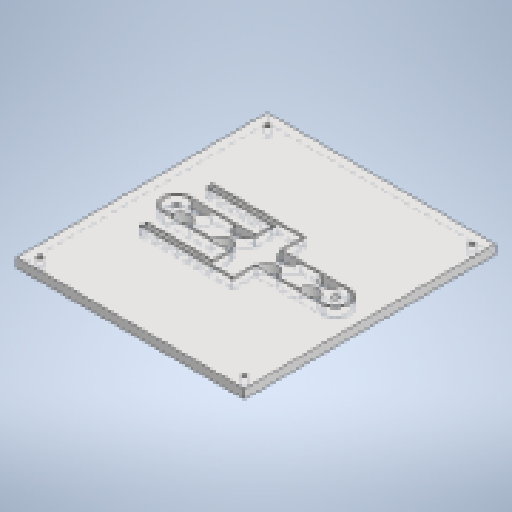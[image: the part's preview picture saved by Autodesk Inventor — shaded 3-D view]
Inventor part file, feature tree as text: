
AUTODESK INVENTOR PART (.ipt)
format: ipt  version: 2023 (Build 270158000, 158)  size: 327,168 bytes
history: native  units: mm
features: extrude x4, thread x4, sketch x4
ambient origin geometry x8: Origin, YZ Plane, XZ Plane, XY Plane, X Axis, Y Axis, Z Axis, Center Point
bodies: Solid1 (feature_tree)
feature tree (12):
  extrude  "Extrusion1"  Depth=100.0mm
  extrude  "Extrusion4"  Depth=5.0mm
  thread  "Thread7"  [1 undecoded]
  thread  "Thread8"  [1 undecoded]
  thread  "Thread9"  [1 undecoded]
  thread  "Thread10"  [1 undecoded]
  extrude  "Extrusion5"  Depth=10.0mm TaperAngle=0.0deg
  extrude  "Extrusion6"  Depth=10.0mm
  sketch  "Sketch1"  dims[d0=110.0mm d1=100.0mm]
  sketch  "Sketch5"  dims[d2=4.0mm d3=0.0mm d41=5.0mm d42=5.0mm d43=2.2mm d44=10.0mm d45=0.0mm d46=10.0mm d47=0.0mm]
  sketch  "Sketch6"  dims[d48=10.0mm d49=0.0mm d50=10.0mm d51=0.0mm]
  sketch  "Sketch8"  dims[d52=10.0mm d53=0.0mm d66=10.0mm d91=12.0mm d92=4.0mm d93=0.0mm d103=1.0mm d113=50.0mm d114=55.0mm d115=5.0mm d116=60.0mm d117=1.0mm d118=2.0mm d119=40.0mm d120=27.5mm d121=40.0mm d122=1.0mm d123=5.0mm d124=0.0mm d125=5.0mm d126=27.5mm d127=1.0mm d128=1.0mm d129=1.0mm d130=1.0mm d131=5.0mm d132=5.0mm d133=0.0mm d134=19.5mm d135=70.0mm d136=5.0mm d138=5.0mm d139=2.2mm d140=2.2mm d141=40.0mm d142=1.0mm d143=1.0mm d144=4.0mm d145=4.0mm d146=3.0mm d147=3.0mm d148=3.0mm d149=4.0mm d150=4.0mm d151=1.0mm d152=2.0mm d153=5.0mm d154=5.0mm d155=5.0mm d156=5.0mm d157=30.0mm d158=1.0mm d159=1.0mm d160=1.0mm d161=1.0mm d162=1.0mm d163=4.0mm d164=0.0mm]
note: 4 required parameter values undecoded (feature->parameter linkage not recoverable at this tier; creation-order binding heuristic only, values carry confidence <= 0.55)
